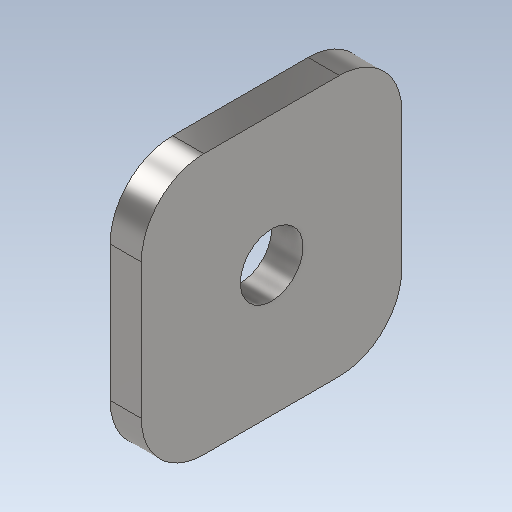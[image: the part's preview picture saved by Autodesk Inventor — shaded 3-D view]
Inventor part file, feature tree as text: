
AUTODESK INVENTOR PART (.ipt)
format: ipt  version: 2021 (Build 250183000, 183)  size: 135,680 bytes
history: native  units: mm
features: sketch x2, extrude x1, hole x1, fillet x1
ambient origin geometry x8: Origin, YZ Plane, XZ Plane, XY Plane, X Axis, Y Axis, Z Axis, Center Point
bodies: Solid1 (feature_tree)
feature tree (5):
  extrude  "Extrusion1"  Depth=50.0mm
  hole  "Hole1"  [1 undecoded]
  fillet  "Fillet2"  Radius=6.0mm
  sketch  "Sketch1"  dims[d0=50.0mm d1=50.0mm]
  sketch  "Sketch2"  dims[d2=25.0mm d3=25.0mm d4=6.0mm d5=0.0mm d6=12.0mm d7=6.0mm d8=4.0mm d9=2.0mm d10=90.0deg d11=8.0mm d12=20.594885mm d14=12.0mm]
note: 1 required parameter value undecoded (feature->parameter linkage not recoverable at this tier; creation-order binding heuristic only, values carry confidence <= 0.55)
